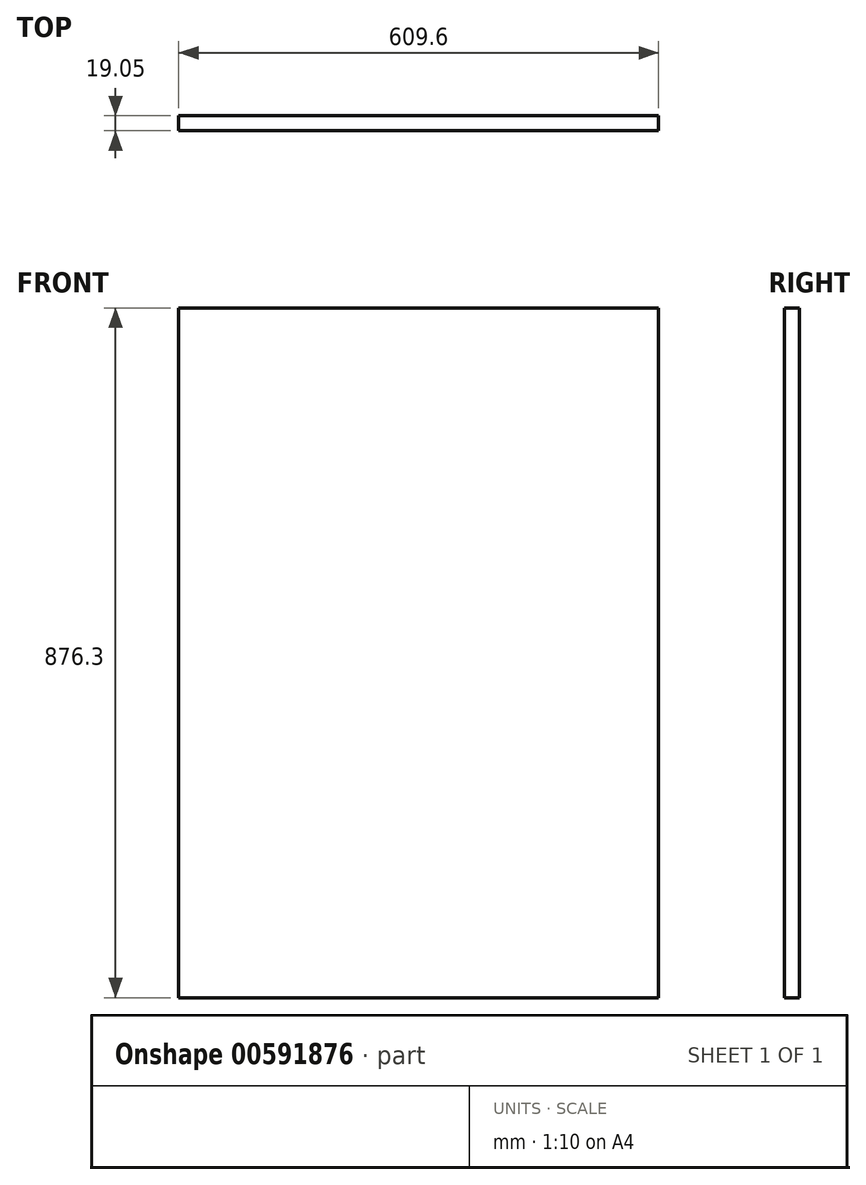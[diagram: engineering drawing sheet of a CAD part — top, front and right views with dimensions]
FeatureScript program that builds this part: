
annotation { "Feature Type Name" : "Feature", "Feature Type Description" : "" }
export const myFeature = defineFeature(function(context is Context, id is Id, definition is map)
    precondition{}
    {
        {
            var Q0;
            Q0=qCreatedBy(makeId("Front.planeOp"),FACE);
            var sketch = newSketch(context, id + "F0", { "sketchPlane" : qUnion([Q0])});
            skLineSegment(sketch, "E0.bottom", {"start": v(304.8, 438.15) * mm, "end": v(-304.8, 438.15) * mm});
            skLineSegment(sketch, "E0.top", {"start": v(304.8, -438.15) * mm, "end": v(-304.8, -438.15) * mm});
            skLineSegment(sketch, "E0.left", {"start": v(304.8, 438.15) * mm, "end": v(304.8, -438.15) * mm});
            skLineSegment(sketch, "E0.right", {"start": v(-304.8, 438.15) * mm, "end": v(-304.8, -438.15) * mm});
            skPoint(sketch, "E0.middle", {"position": v(0, 0) * mm});
            skSolve(sketch);
        }
        {
            var Q0;
            Q0=makeQuery(id+"F0.imprint","IMPRINT",FACE,{"disambiguationData":[TD([[makeQuery(id+"F0.imprint","IMPRINT",EDGE,{"derivedFrom":sQuery(id+"F0.wireOp",EDGE,"E0.bottom")}),1.0]])]});
            extrude(context, id + "F1", {"entities" : qUnion([Q0]), "depth" : 19.05 * mm, "offsetDistance" : 25.4 * mm});
        }
    });
